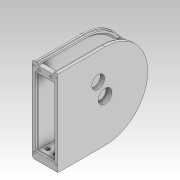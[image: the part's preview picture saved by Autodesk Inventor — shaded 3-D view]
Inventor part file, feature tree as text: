
AUTODESK INVENTOR PART (.ipt)
format: ipt  version: 2020 (Build 240168000, 168)  size: 1,259,008 bytes
history: native  units: mm
features: sketch x50, extrude x47, plane x8, projected_geometry x7, fillet x6, revolve x3, pattern_circular x2, chamfer x2, loft x1, mirror x1, other x1
ambient origin geometry x8: Origin, YZ Plane, XZ Plane, XY Plane, X Axis, Y Axis, Z Axis, Center Point
bodies: Solid1 (feature_tree)
feature tree (128):
  extrude  "Extrusion1"  Depth=250.0mm
  extrude  "Extrusion2"  Depth=100.0mm TaperAngle=0.0deg
  extrude  "Extrusion3"  TaperAngle=0.0deg  [1 undecoded]
  extrude  "Extrusion4"  Depth=10.0mm
  extrude  "Extrusion5"  Depth=1.0mm
  pattern_circular  "Circular Pattern1"  Count=8 Angle=360.0deg
  plane  "Work Plane1"
  plane  "Work Plane2"
  extrude  "Extrusion6"  Depth=30.0mm
  extrude  "Extrusion7"  Depth=10.0mm
  extrude  "Extrusion8"  Depth=10.0mm
  extrude  "Extrusion9"  [1 undecoded]
  chamfer  "Chamfer1"  Distance=10.0mm
  extrude  "Extrusion13"  Depth=10.0mm TaperAngle=0.0deg
  extrude  "Extrusion14"  Depth=3.0mm TaperAngle=0.0deg
  extrude  "Extrusion15"  Depth=2.0mm
  extrude  "Extrusion16"  Depth=3.0mm
  extrude  "Extrusion17"  Depth=80.0mm
  extrude  "Extrusion18"  Depth=60.0mm
  extrude  "Extrusion19"  Depth=80.0mm TaperAngle=360.0deg
  extrude  "Extrusion20"  Depth=15.5mm TaperAngle=0.0deg
  fillet  "Fillet2"  Radius=22.1mm
  pattern_circular  "Circular Pattern2"  Count=8 Angle=360.0deg
  extrude  "Extrusion21"  Depth=10.0mm
  extrude  "Extrusion22"  Depth=7.0mm
  plane  "Work Plane3"
  revolve  "Revolution1"  [1 undecoded]
  revolve  "Revolution2"  [1 undecoded]
  plane  "Work Plane4"
  extrude  "Extrusion23"  Depth=96.8mm TaperAngle=0.0deg
  extrude  "Extrusion24"  Depth=2.5mm
  fillet  "Fillet3"  Radius=5.2mm
  loft  "Loft1"
  extrude  "Extrusion25"  TaperAngle=90.0deg  [1 undecoded]
  extrude  "Extrusion26"  Depth=25.0mm
  extrude  "Extrusion27"  Depth=25.0mm
  extrude  "Extrusion28"  Depth=2.7mm
  plane  "Work Plane5"
  extrude  "Extrusion29"  Depth=5.5mm
  extrude  "Extrusion30"  TaperAngle=90.0deg  [1 undecoded]
  extrude  "Extrusion32"  Depth=2.0mm TaperAngle=0.0deg
  extrude  "Extrusion35"  Depth=6.0mm
  revolve  "Revolution3"  [1 undecoded]
  extrude  "Extrusion36"  [1 undecoded]
  plane  "Work Plane7"
  extrude  "Extrusion37"  Depth=1.0mm TaperAngle=0.0deg
  extrude  "Extrusion38"  Depth=5.0mm
  mirror  "Mirror1"
  extrude  "Extrusion39"  TaperAngle=0.0deg  [1 undecoded]
  extrude  "Extrusion40"  Depth=3.0mm
  extrude  "Extrusion41"  Depth=10.0mm
  chamfer  "Chamfer3"  [1 undecoded]
  fillet  "Fillet5"  [1 undecoded]
  extrude  "Extrusion42"  Depth=65.0mm TaperAngle=0.0deg
  extrude  "Extrusion43"  Depth=5.0mm
  plane  "Work Plane8"
  extrude  "Extrusion44"  Depth=65.0mm
  plane  "Work Plane9"
  extrude  "Extrusion45"  Depth=65.0mm TaperAngle=0.0deg
  extrude  "Extrusion46"  Depth=65.0mm
  fillet  "Fillet8"  Radius=1.0mm
  fillet  "Fillet6"  Radius=3.0mm
  fillet  "Fillet7"  [1 undecoded]
  extrude  "Extrusion47"  Depth=1.0mm
  extrude  "Extrusion48"  TaperAngle=90.0deg  [1 undecoded]
  extrude  "Extrusion49"  Depth=65.0mm
  extrude  "Extrusion50"  Depth=65.0mm
  extrude  "Extrusion51"  Depth=65.0mm TaperAngle=360.0deg
  extrude  "Extrusion52"  Depth=65.0mm TaperAngle=0.0deg
  extrude  "Extrusion53"  Depth=65.0mm
  sketch  "Sketch1"  dims[d0=50.0mm d1=250.0mm]
  sketch  "Sketch2"  dims[d2=50.0mm d3=100.0mm d4=0.0mm]
  sketch  "Sketch4"  dims[d5=5.0mm d7=0.0mm d8=0.0mm]
  sketch  "Sketch5"  dims[d11=10.0mm d12=0.0mm d14=85.0mm]
  sketch  "Sketch7"  dims[d15=1.0mm d16=0.0mm d17=30.0mm]
  projected_geometry  "Projected Loop1"
  sketch  "Sketch8"  dims[d18=3.3mm]
  projected_geometry  "Projected Loop2"
  projected_geometry  "Projected Loop4"
  sketch  "Sketch9"  dims[d19=15.0mm d20=0.0mm d21=80.0mm d22=360.0deg]
  sketch  "Sketch10"  dims[d24=30.0mm d25=30.0mm]
  sketch  "Sketch14"  dims[d30=-5.0mm d31=10.0mm]
  sketch  "Sketch15"  dims[d32=10.0mm d33=10.0mm]
  sketch  "Sketch16"  dims[d34=31.5mm d35=0.0mm d36=-5.0mm d38=10.0mm d39=0.0mm]
  sketch  "Sketch17"  dims[d40=22.1mm d41=10.0mm d42=0.0mm]
  sketch  "Sketch18"  dims[d43=5.0mm d44=3.0mm d45=0.0mm]
  sketch  "Sketch19"  dims[d56=3.0mm d57=2.0mm d58=45.0deg d62=95.1mm]
  sketch  "Sketch20"  dims[d63=10.0mm d64=0.0mm d65=3.0mm]
  sketch  "Sketch21"  dims[d66=0.5mm d67=0.0mm d68=80.0mm]
  sketch  "Sketch22"  dims[d69=16.5mm d70=0.0mm d71=60.0mm]
  sketch  "Sketch23"  dims[d72=3.2mm d73=80.0mm d75=360.0deg]
  other  "Work Axis1"
  sketch  "Sketch24"  dims[d77=15.5mm d78=0.0mm d79=15.5mm d80=0.0mm d81=22.1mm]
  projected_geometry  "Projected Loop5"
  projected_geometry  "Projected Loop6"
  sketch  "Sketch26"  dims[d82=0.0mm d83=0.0mm]
  sketch  "Sketch27"  dims[d84=76.0mm]
  sketch  "Sketch28"  dims[d85=0.1mm d86=0.0mm]
  sketch  "Sketch29"  dims[d87=15.0mm]
  sketch  "Sketch30"  dims[d88=2.0mm]
  sketch  "Sketch31"  dims[d89=22.5mm]
  sketch  "Sketch32"  dims[d90=0.8mm d91=0.0mm]
  sketch  "Sketch33"  dims[d92=0.2mm d93=80.0mm d94=360.0deg]
  projected_geometry  "Projected Loop7"
  sketch  "Sketch34"  dims[d96=24.43461mm d97=10.0mm]
  sketch  "Sketch35"  dims[d98=6.1mm d99=7.0mm]
  sketch  "Sketch38"  dims[d100=6.1mm d101=7.0mm]
  sketch  "Sketch41"  dims[d102=5.0mm d103=0.0mm d104=25.0mm]
  sketch  "Sketch42"  dims[d105=16.1mm d106=96.8mm d107=0.0mm]
  sketch  "Sketch43"  dims[d108=0.0mm d109=2.5mm d110=5.2mm]
  sketch  "Sketch44"  dims[d111=1.0mm d112=5.0mm]
  sketch  "Sketch45"  dims[d113=5.2mm d114=90.0deg]
  sketch  "Sketch46"  dims[d115=15.0mm d116=25.0mm]
  sketch  "Sketch47"  dims[d117=25.0mm d118=19.0mm]
  projected_geometry  "Projected Loop8"
  sketch  "Sketch48"  dims[d119=19.0mm d120=2.7mm]
  sketch  "Sketch49"  dims[d122=4.0mm d123=0.0mm d124=5.5mm]
  sketch  "Sketch50"  dims[d125=2.0mm d126=0.0mm d127=90.0deg]
  sketch  "Sketch51"  dims[d128=2.0mm d129=18.8mm d130=0.0mm]
  sketch  "Sketch52"  dims[d131=111.25mm d132=0.0mm d133=6.0mm]
  sketch  "Sketch53"  dims[d134=4.0mm d135=0.0mm d136=1.0mm]
  sketch  "Sketch54"  dims[d137=1.0mm d138=0.0mm d139=-7.0mm]
  sketch  "Sketch55"  dims[d140=1.0mm d141=1.0mm d142=0.0mm]
  sketch  "Sketch56"  dims[d143=7.0mm d144=5.0mm]
  sketch  "Sketch57"  dims[d145=6.0mm d146=0.0mm d147=90.0deg]
  sketch  "Sketch58"  dims[d148=0.0mm d149=90.0deg d150=3.0mm]
  sketch  "Sketch59"  dims[d151=10.0mm d152=0.0mm d155=110.0mm d156=0.0mm d157=0.0mm d159=30.0deg]
  sketch  "Sketch60"  dims[d160=6.0mm d177=255.0mm d178=0.0mm d179=5.0mm d180=2.1mm d181=52.0mm d182=0.0mm d183=16.1mm d184=1.0mm d185=3.0mm d186=30.0deg d187=1.0mm d188=90.0deg d189=60.0mm d190=3.5mm d191=80.0mm d193=360.0deg d195=52.0mm d196=0.0mm d197=8.0mm d198=0.5mm d199=0.0mm d200=6.0mm d201=1.7mm d202=0.0mm d203=15.0mm d204=20.0mm d205=10.0mm d206=0.0mm d207=1.0mm d208=22.0mm d209=2.0mm d210=0.0mm d211=0.0mm d212=2.0mm d213=2.0mm d214=0.0mm d215=2.0mm d216=2.0mm d217=45.0deg d218=3.0mm d219=5.0mm d220=2.0mm d221=0.0mm d223=30.0mm d224=3.5mm d225=32.0mm d226=0.0mm d227=-6.0mm d229=32.0mm d230=0.0mm d231=12.0mm d232=-17.0mm d233=2.0mm d234=3.0mm d235=30.0mm d237=30.0mm d238=10.0mm d240=10.0mm d242=10.0mm d243=11.0mm d244=0.0mm d245=7.0mm d246=102.5mm d247=0.0mm d248=3.0mm d249=1.0mm d250=3.0mm d251=55.0mm d252=0.0mm d253=0.0mm d254=1.3mm d255=1.3mm d256=1.3mm d257=10.5mm d258=2.0mm d259=0.0mm d260=10.0mm d261=0.0mm d262=10.0mm d263=0.0mm d264=2.0mm d265=8.0mm d266=3.0mm d267=3.0mm d268=3.2mm d269=5.0mm d270=0.0mm d271=10.0mm d272=5.0mm d273=8.0mm d274=7.0mm d275=0.0mm d276=2.5mm d277=2.5mm d278=2.0mm d279=5.0mm d280=7.0mm d281=65.0mm d282=0.0mm]
note: 13 required parameter values undecoded (feature->parameter linkage not recoverable at this tier; creation-order binding heuristic only, values carry confidence <= 0.55)